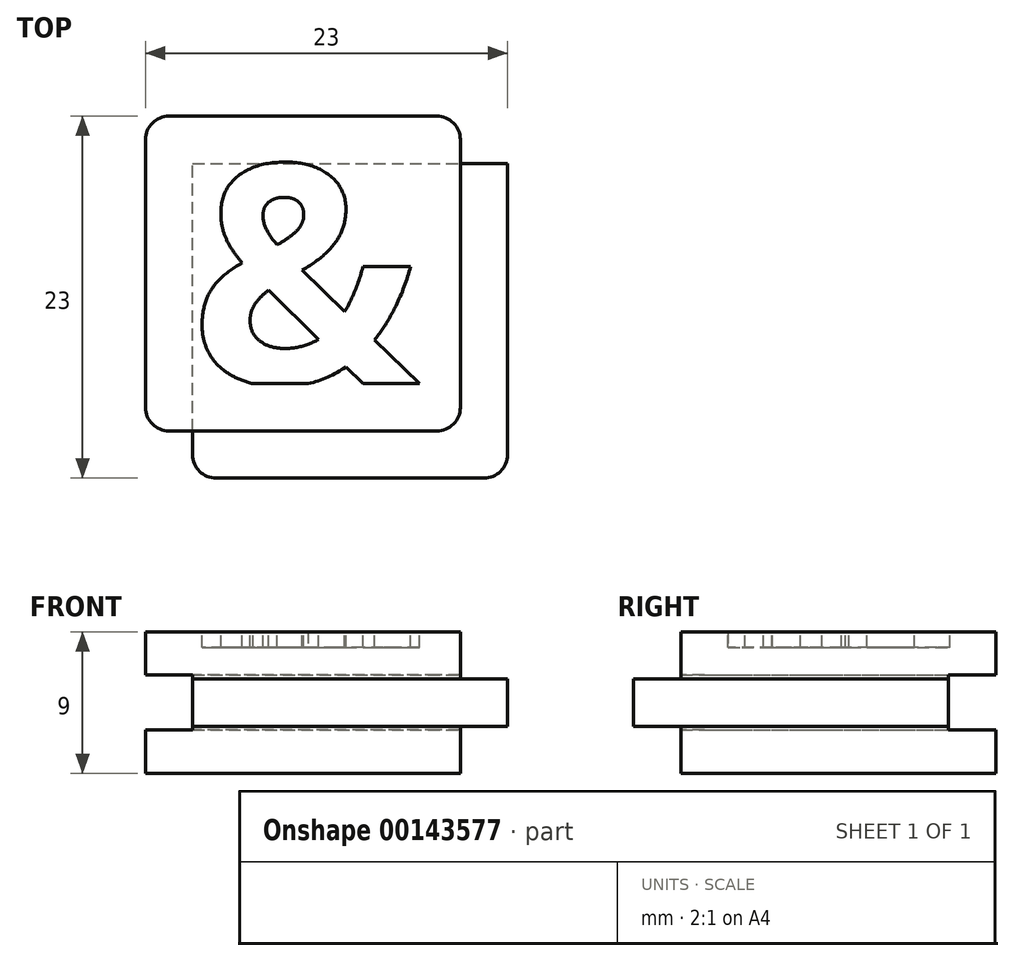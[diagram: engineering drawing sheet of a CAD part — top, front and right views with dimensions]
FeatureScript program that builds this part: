
annotation { "Feature Type Name" : "Feature", "Feature Type Description" : "" }
export const myFeature = defineFeature(function(context is Context, id is Id, definition is map)
    precondition{}
    {
        {
            var Q0;
            Q0=qCreatedBy(makeId("Front.planeOp"),FACE);
            var sketch = newSketch(context, id + "F0", { "sketchPlane" : qUnion([Q0])});
            skLineSegment(sketch, "E0.bottom", {"start": v(10, 4.5) * mm, "end": v(-10, 4.5) * mm});
            skLineSegment(sketch, "E0.top", {"start": v(10, -4.5) * mm, "end": v(-10, -4.5) * mm});
            skLineSegment(sketch, "E0.left", {"start": v(10, 4.5) * mm, "end": v(10, -4.5) * mm});
            skLineSegment(sketch, "E0.right", {"start": v(-10, 4.5) * mm, "end": v(-10, -4.5) * mm});
            skPoint(sketch, "E0.middle", {"position": v(0, 0) * mm});
            skLineSegment(sketch, "E1.bottom", {"start": v(13, 1.5) * mm, "end": v(7, 1.5) * mm});
            skLineSegment(sketch, "E1.top", {"start": v(13, -1.5) * mm, "end": v(7, -1.5) * mm});
            skLineSegment(sketch, "E1.left", {"start": v(13, 1.5) * mm, "end": v(13, -1.5) * mm});
            skLineSegment(sketch, "E1.right", {"start": v(7, 1.5) * mm, "end": v(7, -1.5) * mm});
            skPoint(sketch, "E1.middle", {"position": v(10, 0) * mm});
            skLineSegment(sketch, "E2.bottom", {"start": v(7, 1.5) * mm, "end": v(-7, 1.5) * mm});
            skLineSegment(sketch, "E2.top", {"start": v(7, -1.5) * mm, "end": v(-7, -1.5) * mm});
            skLineSegment(sketch, "E2.right", {"start": v(-7, 1.5) * mm, "end": v(-7, -1.5) * mm});
            skLineSegment(sketch, "E3.bottom", {"start": v(-7, -1.5) * mm, "end": v(-10, -1.5) * mm});
            skLineSegment(sketch, "E3.top", {"start": v(-7, 1.5) * mm, "end": v(-10, 1.5) * mm});
            skLineSegment(sketch, "E3.left", {"start": v(-7, -1.5) * mm, "end": v(-7, 1.5) * mm});
            skLineSegment(sketch, "E3.right", {"start": v(-10, -1.5) * mm, "end": v(-10, 1.5) * mm});
            skSolve(sketch);
        }
        {
            var Q0;
            {var subQ5=sQuery(id+"F0.wireOp",EDGE,"E0.bottom");Q0=makeQuery(id+"F0.imprint","IMPRINT",FACE,{"disambiguationData":[TD([[makeQuery(id+"F0.imprint","IMPRINT",EDGE,{"derivedFrom":subQ5}),1.0]])]});}
            var Q1;
            Q1=makeQuery(id+"F0.imprint","IMPRINT",FACE,{"disambiguationData":[TD([[makeQuery(id+"F0.imprint","IMPRINT",EDGE,{"derivedFrom":sQuery(id+"F0.wireOp",EDGE,"E2.bottom")}),1.0]])]});
            var Q2;
            {var subQ5=sQuery(id+"F0.wireOp",EDGE,"E1.left");Q2=makeQuery(id+"F0.imprint","IMPRINT",FACE,{"disambiguationData":[TD([[makeQuery(id+"F0.imprint","IMPRINT",EDGE,{"derivedFrom":subQ5}),-1.0]])]});}
            var Q3;
            {var subQ5=sQuery(id+"F0.wireOp",EDGE,"E1.right");Q3=makeQuery(id+"F0.imprint","IMPRINT",FACE,{"disambiguationData":[TD([[makeQuery(id+"F0.imprint","IMPRINT",EDGE,{"derivedFrom":subQ5}),1.0]])]});}
            var Q4;
            Q4=makeQuery(id+"F0.imprint","IMPRINT",FACE,{"disambiguationData":[TD([[makeQuery(id+"F0.imprint","IMPRINT",EDGE,{"derivedFrom":sQuery(id+"F0.wireOp",EDGE,"E3.bottom")}),-1.0]])]});
            var Q5;
            {var subQ5=sQuery(id+"F0.wireOp",EDGE,"E0.top");Q5=makeQuery(id+"F0.imprint","IMPRINT",FACE,{"disambiguationData":[TD([[makeQuery(id+"F0.imprint","IMPRINT",EDGE,{"derivedFrom":subQ5}),-1.0]])]});}
            extrude(context, id + "F1", {"entities" : qUnion([Q0, Q1, Q2, Q3, Q4, Q5]), "oppositeDirection" : true, "depth" : 20 * mm});
        }
        {
            var Q0;
            Q0=makeQuery(id+"F0.imprint","IMPRINT",FACE,{"disambiguationData":[TD([[makeQuery(id+"F0.imprint","IMPRINT",EDGE,{"derivedFrom":sQuery(id+"F0.wireOp",EDGE,"E3.bottom")}),-1.0]])]});
            var Q1;
            Q1=makeQuery(id+"F0.imprint","IMPRINT",FACE,{"disambiguationData":[TD([[makeQuery(id+"F0.imprint","IMPRINT",EDGE,{"derivedFrom":sQuery(id+"F0.wireOp",EDGE,"E2.bottom")}),1.0]])]});
            var Q2;
            {var subQ5=sQuery(id+"F0.wireOp",EDGE,"E1.right");Q2=makeQuery(id+"F0.imprint","IMPRINT",FACE,{"disambiguationData":[TD([[makeQuery(id+"F0.imprint","IMPRINT",EDGE,{"derivedFrom":subQ5}),1.0]])]});}
            var Q3;
            {var subQ5=sQuery(id+"F0.wireOp",EDGE,"E1.left");Q3=makeQuery(id+"F0.imprint","IMPRINT",FACE,{"disambiguationData":[TD([[makeQuery(id+"F0.imprint","IMPRINT",EDGE,{"derivedFrom":subQ5}),-1.0]])]});}
            extrude(context, id + "F2", {"entities" : qUnion([Q0, Q1, Q2, Q3]), "operationType" : NewBodyOperationType.ADD, "depth" : 3 * mm});
        }
        {
            var Q0;
            {var subQ0=sQuery(id+"F0.wireOp",EDGE,"E1.left");Q0=makeQuery(id+"F2.boolean.opBoolean","MERGE",FACE,{"derivedFrom":[makeQuery(id+"F1.opExtrude","SWEPT_FACE",FACE,{"disambiguationData":[OSD([subQ0])]}),makeQuery(id+"F2.opExtrude","SWEPT_FACE",FACE,{"disambiguationData":[OSD([subQ0])]})]});}
            var sketch = newSketch(context, id + "F3", { "sketchPlane" : qUnion([Q0])});
            skLineSegment(sketch, "E4.bottom", {"start": v(23, 1.75) * mm, "end": v(17, 1.75) * mm});
            skLineSegment(sketch, "E4.top", {"start": v(23, -1.75) * mm, "end": v(17, -1.75) * mm});
            skLineSegment(sketch, "E4.left", {"start": v(23, 1.75) * mm, "end": v(23, -1.75) * mm});
            skLineSegment(sketch, "E4.right", {"start": v(17, 1.75) * mm, "end": v(17, -1.75) * mm});
            skPoint(sketch, "E4.middle", {"position": v(20, 0) * mm});
            skSolve(sketch);
        }
        {
            var Q0;
            {var subQ1=sQuery(id+"F3.wireOp",EDGE,"E4.bottom");Q0=makeQuery(id+"F3.imprint","IMPRINT",FACE,{"disambiguationData":[TD([[makeQuery(id+"F3.imprint","IMPRINT",EDGE,{"derivedFrom":subQ1}),1.0]])]});}
            var Q1;
            {var subQ1=sQuery(id+"F0.wireOp",EDGE,"E1.left");var subQ8=makeQuery(id+"F1.opExtrude","CAP_EDGE",EDGE,{"disambiguationData":[OSD([subQ1])],"isStart":false});Q1=makeQuery(id+"F3.imprint","IMPRINT",FACE,{"disambiguationData":[TD([[makeQuery(id+"F3.imprint","IMPRINT",EDGE,{"derivedFrom":subQ8}),-1.0]])]});}
            extrude(context, id + "F4", {"entities" : qUnion([Q0, Q1]), "operationType" : NewBodyOperationType.REMOVE, "oppositeDirection" : true, "depth" : 100 * mm});
        }
        {
            var Q0;
            Q0=makeQuery(id+"F4.boolean.opBoolean","COPY",FACE,{"derivedFrom":makeQuery(id+"F4.opExtrude","SWEPT_FACE",FACE,{"disambiguationData":[OSD([sQuery(id+"F3.wireOp",EDGE,"E4.right")])]})});
            var sketch = newSketch(context, id + "F5", { "sketchPlane" : qUnion([Q0])});
            skLineSegment(sketch, "E5.bottom", {"start": v(13, 1.75) * mm, "end": v(7, 1.75) * mm});
            skLineSegment(sketch, "E5.top", {"start": v(13, -1.75) * mm, "end": v(7, -1.75) * mm});
            skLineSegment(sketch, "E5.left", {"start": v(13, 1.75) * mm, "end": v(13, -1.75) * mm});
            skLineSegment(sketch, "E5.right", {"start": v(7, 1.75) * mm, "end": v(7, -1.75) * mm});
            skPoint(sketch, "E5.middle", {"position": v(10, 0) * mm});
            skSolve(sketch);
        }
        {
            var Q0;
            {var subQ3=sQuery(id+"F5.wireOp",EDGE,"E5.left");Q0=makeQuery(id+"F5.imprint","IMPRINT",FACE,{"disambiguationData":[TD([[makeQuery(id+"F5.imprint","IMPRINT",EDGE,{"derivedFrom":subQ3}),-1.0]])]});}
            var Q1;
            {var subQ4=sQuery(id+"F5.wireOp",EDGE,"E5.right");Q1=makeQuery(id+"F5.imprint","IMPRINT",FACE,{"disambiguationData":[TD([[makeQuery(id+"F5.imprint","IMPRINT",EDGE,{"derivedFrom":subQ4}),1.0]])]});}
            extrude(context, id + "F6", {"entities" : qUnion([Q0, Q1]), "operationType" : NewBodyOperationType.REMOVE, "oppositeDirection" : true, "depth" : 100 * mm});
        }
        {
            var Q0;
            Q0=makeQuery(id+"F6.boolean.opBoolean","INTERSECT",EDGE,{"derivedFrom":[makeQuery(id+"F2.opExtrude","CAP_FACE",FACE,{"disambiguationData":[OSD([sQuery(id+"F0.wireOp",EDGE,"E1.bottom"),sQuery(id+"F0.wireOp",EDGE,"E1.top"),sQuery(id+"F0.wireOp",EDGE,"E1.left"),sQuery(id+"F0.wireOp",EDGE,"E2.bottom"),sQuery(id+"F0.wireOp",EDGE,"E2.top"),sQuery(id+"F0.wireOp",EDGE,"E3.bottom"),sQuery(id+"F0.wireOp",EDGE,"E3.top"),sQuery(id+"F0.wireOp",EDGE,"E3.right")])],"isStart":false}),makeQuery(id+"F6.opExtrude","SWEPT_FACE",FACE,{"disambiguationData":[OSD([sQuery(id+"F5.wireOp",EDGE,"E5.right")])]})]});
            var Q1;
            Q1=makeQuery(id+"F2.opExtrude","CAP_EDGE",EDGE,{"disambiguationData":[OSD([sQuery(id+"F0.wireOp",EDGE,"E1.left")])],"isStart":false});
            var Q2;
            {var subQ0=sQuery(id+"F0.wireOp",EDGE,"E0.left");Q2=makeQuery(id+"F1.opExtrude","CAP_EDGE",EDGE,{"disambiguationData":[OSD([subQ0]),TDD([makeQuery(id+"F0.imprint","IMPRINT",EDGE,{"disambiguationData":[TD([[makeQuery(id+"F0.imprint","INTERSECT",VERTEX,{"derivedFrom":[sQuery(id+"F0.wireOp",EDGE,"E0.bottom"),subQ0]}),-1.0]])],"derivedFrom":subQ0})])],"isStart":true});}
            var Q3;
            {var subQ0=sQuery(id+"F0.wireOp",EDGE,"E0.left");Q3=makeQuery(id+"F1.opExtrude","CAP_EDGE",EDGE,{"disambiguationData":[OSD([subQ0]),TDD([makeQuery(id+"F0.imprint","IMPRINT",EDGE,{"disambiguationData":[TD([[makeQuery(id+"F0.imprint","INTERSECT",VERTEX,{"derivedFrom":[sQuery(id+"F0.wireOp",EDGE,"E0.top"),subQ0]}),1.0]])],"derivedFrom":subQ0})])],"isStart":true});}
            var Q4;
            {var subQ0=sQuery(id+"F0.wireOp",EDGE,"E3.right");var subQ1=sQuery(id+"F0.wireOp",EDGE,"E0.right");var subQ3=sQuery(id+"F0.wireOp",EDGE,"E0.top");Q4=makeQuery(id+"F2.boolean.opBoolean","SPLIT",EDGE,{"disambiguationData":[TD([makeQuery(id+"F1.opExtrude","SWEPT_FACE",FACE,{"disambiguationData":[OSD([subQ3])]})])],"derivedFrom":makeQuery(id+"F1.opExtrude","CAP_EDGE",EDGE,{"disambiguationData":[OSD([subQ1,subQ0])],"isStart":true})});}
            var Q5;
            {var subQ1=sQuery(id+"F0.wireOp",EDGE,"E3.right");var subQ2=sQuery(id+"F0.wireOp",EDGE,"E0.right");var subQ3=sQuery(id+"F0.wireOp",EDGE,"E0.bottom");Q5=makeQuery(id+"F2.boolean.opBoolean","SPLIT",EDGE,{"disambiguationData":[TD([makeQuery(id+"F1.opExtrude","SWEPT_FACE",FACE,{"disambiguationData":[OSD([subQ3])]})])],"derivedFrom":makeQuery(id+"F1.opExtrude","CAP_EDGE",EDGE,{"disambiguationData":[OSD([subQ2,subQ1])],"isStart":true})});}
            var Q6;
            Q6=makeQuery(id+"F6.boolean.opBoolean","COPY",EDGE,{"derivedFrom":makeQuery(id+"F6.opExtrude","CAP_EDGE",EDGE,{"disambiguationData":[OSD([sQuery(id+"F5.wireOp",EDGE,"E5.right")])],"isStart":true})});
            var Q7;
            {var subQ0=sQuery(id+"F0.wireOp",EDGE,"E3.right");var subQ1=sQuery(id+"F0.wireOp",EDGE,"E0.right");var subQ2=sQuery(id+"F0.wireOp",EDGE,"E0.bottom");Q7=makeQuery(id+"F4.boolean.opBoolean","SPLIT",EDGE,{"disambiguationData":[TD([makeQuery(id+"F1.opExtrude","SWEPT_FACE",FACE,{"disambiguationData":[OSD([subQ2])]})])],"derivedFrom":makeQuery(id+"F1.opExtrude","CAP_EDGE",EDGE,{"disambiguationData":[OSD([subQ1,subQ0])],"isStart":false})});}
            var Q8;
            {var subQ0=sQuery(id+"F0.wireOp",EDGE,"E3.right");var subQ1=sQuery(id+"F0.wireOp",EDGE,"E0.right");var subQ2=sQuery(id+"F0.wireOp",EDGE,"E0.top");Q8=makeQuery(id+"F4.boolean.opBoolean","SPLIT",EDGE,{"disambiguationData":[TD([makeQuery(id+"F1.opExtrude","SWEPT_FACE",FACE,{"disambiguationData":[OSD([subQ2])]})])],"derivedFrom":makeQuery(id+"F1.opExtrude","CAP_EDGE",EDGE,{"disambiguationData":[OSD([subQ1,subQ0])],"isStart":false})});}
            var Q9;
            Q9=makeQuery(id+"F4.boolean.opBoolean","COPY",EDGE,{"derivedFrom":makeQuery(id+"F4.opExtrude","CAP_EDGE",EDGE,{"disambiguationData":[OSD([sQuery(id+"F3.wireOp",EDGE,"E4.right")])],"isStart":true})});
            var Q10;
            {var subQ0=sQuery(id+"F0.wireOp",EDGE,"E0.left");Q10=makeQuery(id+"F1.opExtrude","CAP_EDGE",EDGE,{"disambiguationData":[OSD([subQ0]),TDD([makeQuery(id+"F0.imprint","IMPRINT",EDGE,{"disambiguationData":[TD([[makeQuery(id+"F0.imprint","INTERSECT",VERTEX,{"derivedFrom":[sQuery(id+"F0.wireOp",EDGE,"E0.bottom"),subQ0]}),-1.0]])],"derivedFrom":subQ0})])],"isStart":false});}
            var Q11;
            {var subQ0=sQuery(id+"F0.wireOp",EDGE,"E0.left");Q11=makeQuery(id+"F1.opExtrude","CAP_EDGE",EDGE,{"disambiguationData":[OSD([subQ0]),TDD([makeQuery(id+"F0.imprint","IMPRINT",EDGE,{"disambiguationData":[TD([[makeQuery(id+"F0.imprint","INTERSECT",VERTEX,{"derivedFrom":[sQuery(id+"F0.wireOp",EDGE,"E0.top"),subQ0]}),1.0]])],"derivedFrom":subQ0})])],"isStart":false});}
            fillet(context, id + "F7", {"entities" : qUnion([Q0, Q1, Q2, Q3, Q4, Q5, Q6, Q7, Q8, Q9, Q10, Q11]), "radius" : 1.5 * mm, "tangentPropagation" : true, "allowEdgeOverflow" : false});
        }
        {
            var Q0;
            Q0=makeQuery(id+"F1.opExtrude","SWEPT_FACE",FACE,{"disambiguationData":[OSD([sQuery(id+"F0.wireOp",EDGE,"E0.bottom")])]});
            var sketch = newSketch(context, id + "F8", { "sketchPlane" : qUnion([Q0])});
            skText(sketch, "E6", { "text": "&", "fontName": "OpenSans-Bold.ttf"});
            skLineSegment(sketch, "E7.0", {"start": v(12.55, 3) * mm, "end": v(-11.07, 3) * mm});
            const initialGuessF8  = {"E6": [-0.00718, 0.003, 1, 0, 0.014]};
            skSetInitialGuess(sketch, initialGuessF8);
            skSolve(sketch);
        }
        {
            var Q0;
            {var subQ6=sQuery(id+"F8.wireOp",EDGE,"E6.sketch_text.stroke-1");Q0=makeQuery(id+"F8.imprint","IMPRINT",FACE,{"disambiguationData":[TD([[makeQuery(id+"F8.imprint","IMPRINT",EDGE,{"derivedFrom":subQ6}),-1.0]])]});}
            extrude(context, id + "F9", {"entities" : qUnion([Q0]), "operationType" : NewBodyOperationType.REMOVE, "oppositeDirection" : true, "depth" : 1 * mm});
        }
    });
